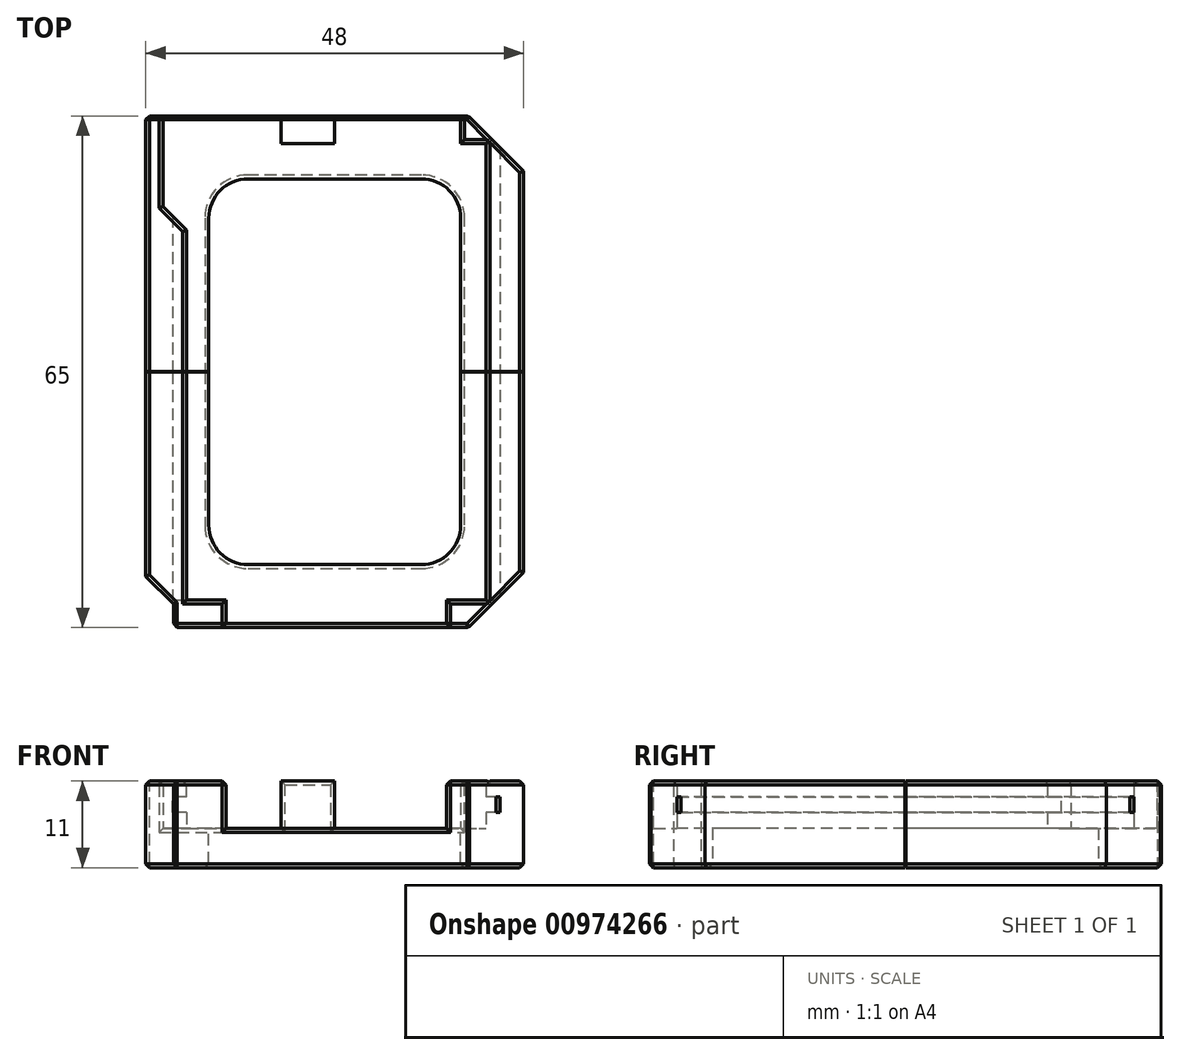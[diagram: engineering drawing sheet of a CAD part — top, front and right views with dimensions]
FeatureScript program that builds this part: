
annotation { "Feature Type Name" : "Feature", "Feature Type Description" : "" }
export const myFeature = defineFeature(function(context is Context, id is Id, definition is map)
    precondition{}
    {
        {
            var Q0;
            Q0=qCreatedBy(makeId("Top.planeOp"),FACE);
            cPlane(context, id + "F0", {"entities" : qUnion([Q0]), "cplaneType" : CPlaneType.OFFSET, "offset" : 7 * mm, "width" : 150 * mm, "height" : 150 * mm});
        }
        {
            var Q0;
            Q0=qCreatedBy(makeId("Top.planeOp"),FACE);
            cPlane(context, id + "F1", {"entities" : qUnion([Q0]), "cplaneType" : CPlaneType.OFFSET, "offset" : 5 * mm, "width" : 150 * mm, "height" : 150 * mm});
        }
        {
            var Q0;
            Q0=qCreatedBy(makeId("Top.planeOp"),FACE);
            cPlane(context, id + "F2", {"entities" : qUnion([Q0]), "cplaneType" : CPlaneType.OFFSET, "offset" : 2 * mm, "oppositeDirection" : true, "width" : 150 * mm, "height" : 150 * mm});
        }
        {
            var Q0;
            Q0=qCreatedBy(makeId("Top.planeOp"),FACE);
            var sketch = newSketch(context, id + "F3", { "sketchPlane" : qUnion([Q0])});
            skLineSegment(sketch, "E0", {"start": v(0, 0) * mm, "end": v(10, 0) * mm, "construction": true});
            skLineSegment(sketch, "E1.bottom", {"start": v(10, 0) * mm, "end": v(13.5, 0) * mm, "construction": true});
            skLineSegment(sketch, "E1.top", {"start": v(10, 65) * mm, "end": v(51, 65) * mm});
            skLineSegment(sketch, "E1.left", {"start": v(10, 0) * mm, "end": v(10, 6.5) * mm, "construction": true});
            skLineSegment(sketch, "E1.right", {"start": v(58, 7) * mm, "end": v(58, 58) * mm});
            skCircle(sketch, "E2", {"center": v(10, 3) * mm, "radius": 3 * mm, "construction": true});
            skLineSegment(sketch, "E3", {"start": v(13.5, 3) * mm, "end": v(13.5, 0) * mm});
            skLineSegment(sketch, "E4", {"start": v(13.5, 3) * mm, "end": v(10, 3) * mm, "construction": true});
            skArc(sketch, "E5", {"start": v(13.5, 3) * mm, "mid": v(12.47, 5.47) * mm, "end": v(10, 6.5) * mm, "construction": true});
            skLineSegment(sketch, "E6", {"start": v(10, 6.5) * mm, "end": v(10, 65) * mm});
            skLineSegment(sketch, "E7", {"start": v(13.5, 0) * mm, "end": v(51, 0) * mm});
            skPoint(sketch, "E8.visualSharp", {"position": v(58, 65) * mm});
            skArc(sketch, "E8.filletArc", {"start": v(58, 58) * mm, "mid": v(55.95, 62.95) * mm, "end": v(51, 65) * mm, "construction": true});
            skPoint(sketch, "E9.visualSharp", {"position": v(58, 0) * mm});
            skArc(sketch, "E9.filletArc", {"start": v(51, 0) * mm, "mid": v(55.95, 2.05) * mm, "end": v(58, 7) * mm, "construction": true});
            skLineSegment(sketch, "E10", {"start": v(51, 65) * mm, "end": v(58, 58) * mm});
            skLineSegment(sketch, "E11", {"start": v(51, 0) * mm, "end": v(58, 7) * mm});
            skLineSegment(sketch, "E12", {"start": v(10, 6.5) * mm, "end": v(13.5, 3) * mm});
            skSolve(sketch);
        }
        {
            var Q0;
            Q0 = qSketchRegion(id + "F3", true);
            extrude(context, id + "F4", {"entities" : qUnion([Q0]), "depth" : 11 * mm, "offsetDistance" : 25 * mm});
        }
        {
            var Q0;
            Q0=qCreatedBy(id+"F2.planeOp",FACE);
            var sketch = newSketch(context, id + "F5", { "sketchPlane" : qUnion([Q0])});
            skLineSegment(sketch, "E13.bottom", {"start": v(18, 57) * mm, "end": v(50, 57) * mm});
            skLineSegment(sketch, "E13.top", {"start": v(18, 8) * mm, "end": v(50, 8) * mm});
            skLineSegment(sketch, "E13.left", {"start": v(18, 57) * mm, "end": v(18, 8) * mm});
            skLineSegment(sketch, "E13.right", {"start": v(50, 57) * mm, "end": v(50, 8) * mm});
            skLineSegment(sketch, "E14.0", {"start": v(13.5, 0) * mm, "end": v(13.5, 0) * mm});
            skLineSegment(sketch, "E15.0", {"start": v(58, 7) * mm, "end": v(58, 7) * mm});
            skLineSegment(sketch, "E16.0", {"start": v(10, 65) * mm, "end": v(10, 65) * mm});
            skSolve(sketch);
        }
        {
            var Q0;
            Q0 = qSketchRegion(id + "F5", true);
            extrude(context, id + "F6", {"entities" : qUnion([Q0]), "operationType" : NewBodyOperationType.REMOVE, "depth" : 25 * mm, "offsetDistance" : 25 * mm});
        }
        {
            var Q0;
            Q0=makeQuery(id+"F6.boolean.opBoolean","COPY",EDGE,{"derivedFrom":makeQuery(id+"F6.opExtrude","SWEPT_EDGE",EDGE,{"disambiguationData":[OSD([sQuery(id+"F5.wireOp",EDGE,"E13.bottom"),sQuery(id+"F5.wireOp",EDGE,"E13.left")])]})});
            var Q1;
            Q1=makeQuery(id+"F6.boolean.opBoolean","COPY",EDGE,{"derivedFrom":makeQuery(id+"F6.opExtrude","SWEPT_EDGE",EDGE,{"disambiguationData":[OSD([sQuery(id+"F5.wireOp",EDGE,"E13.bottom"),sQuery(id+"F5.wireOp",EDGE,"E13.right")])]})});
            var Q2;
            Q2=makeQuery(id+"F6.boolean.opBoolean","COPY",EDGE,{"derivedFrom":makeQuery(id+"F6.opExtrude","SWEPT_EDGE",EDGE,{"disambiguationData":[OSD([sQuery(id+"F5.wireOp",EDGE,"E13.top"),sQuery(id+"F5.wireOp",EDGE,"E13.right")])]})});
            var Q3;
            Q3=makeQuery(id+"F6.boolean.opBoolean","COPY",EDGE,{"derivedFrom":makeQuery(id+"F6.opExtrude","SWEPT_EDGE",EDGE,{"disambiguationData":[OSD([sQuery(id+"F5.wireOp",EDGE,"E13.top"),sQuery(id+"F5.wireOp",EDGE,"E13.left")])]})});
            fillet(context, id + "F7", {"entities" : qUnion([Q0, Q1, Q2, Q3]), "radius" : 5 * mm, "tangentPropagation" : true, "allowEdgeOverflow" : false});
        }
        {
            var Q0;
            Q0=qCreatedBy(id+"F0.planeOp",FACE);
            var sketch = newSketch(context, id + "F8", { "sketchPlane" : qUnion([Q0])});
            skLineSegment(sketch, "E17.bottom", {"start": v(13.4, 61.5) * mm, "end": v(55, 61.5) * mm});
            skLineSegment(sketch, "E17.top", {"start": v(13.4, 3.5) * mm, "end": v(55, 3.5) * mm});
            skLineSegment(sketch, "E17.left", {"start": v(13.4, 61.5) * mm, "end": v(13.4, 3.5) * mm});
            skLineSegment(sketch, "E17.right", {"start": v(55, 61.5) * mm, "end": v(55, 3.5) * mm});
            skSolve(sketch);
        }
        {
            var Q0;
            Q0 = qSketchRegion(id + "F8", true);
            extrude(context, id + "F9", {"entities" : qUnion([Q0]), "operationType" : NewBodyOperationType.REMOVE, "depth" : 2 * mm, "offsetDistance" : 25 * mm});
        }
        {
            var Q0;
            Q0=qCreatedBy(id+"F1.planeOp",FACE);
            var sketch = newSketch(context, id + "F10", { "sketchPlane" : qUnion([Q0])});
            skLineSegment(sketch, "E18.bottom", {"start": v(27.2, 61.5) * mm, "end": v(34, 61.5) * mm});
            skLineSegment(sketch, "E18.top", {"start": v(15.2, 3.5) * mm, "end": v(20.2, 3.5) * mm});
            skLineSegment(sketch, "E18.left", {"start": v(15.2, 50.5) * mm, "end": v(15.2, 3.5) * mm});
            skLineSegment(sketch, "E18.right", {"start": v(53.2, 61.5) * mm, "end": v(53.2, 3.5) * mm});
            skLineSegment(sketch, "E19.0", {"start": v(10, 65) * mm, "end": v(10, 65) * mm});
            skLineSegment(sketch, "E20.0", {"start": v(58, 7) * mm, "end": v(58, 7) * mm});
            skLineSegment(sketch, "E21", {"start": v(12.2, 53.5) * mm, "end": v(12.2, 65.5) * mm});
            skLineSegment(sketch, "E22", {"start": v(12.2, 65.5) * mm, "end": v(27.2, 65.5) * mm});
            skLineSegment(sketch, "E23", {"start": v(27.2, 65.5) * mm, "end": v(27.2, 61.5) * mm});
            skLineSegment(sketch, "E24", {"start": v(34, 61.5) * mm, "end": v(34, 65.5) * mm});
            skLineSegment(sketch, "E25", {"start": v(34, 65.5) * mm, "end": v(50, 65.5) * mm});
            skLineSegment(sketch, "E26", {"start": v(50, 65.5) * mm, "end": v(50, 61.5) * mm});
            skLineSegment(sketch, "E27.trimOffspring", {"start": v(50, 61.5) * mm, "end": v(53.2, 61.5) * mm});
            skLineSegment(sketch, "E28", {"start": v(20.2, 3.5) * mm, "end": v(20.2, -0.5) * mm});
            skLineSegment(sketch, "E29", {"start": v(20.2, -0.5) * mm, "end": v(48.2, -0.5) * mm});
            skLineSegment(sketch, "E30", {"start": v(48.2, -0.5) * mm, "end": v(48.2, 3.5) * mm});
            skLineSegment(sketch, "E31.trimOffspring", {"start": v(48.2, 3.5) * mm, "end": v(53.2, 3.5) * mm});
            skLineSegment(sketch, "E32", {"start": v(12.2, 53.5) * mm, "end": v(15.2, 50.5) * mm});
            skSolve(sketch);
        }
        {
            var Q0;
            Q0 = qSketchRegion(id + "F10", true);
            extrude(context, id + "F11", {"entities" : qUnion([Q0]), "operationType" : NewBodyOperationType.REMOVE, "depth" : 8 * mm, "offsetDistance" : 25 * mm});
        }
        {
            var Q0;
            Q0=makeQuery(id+"F4.opExtrude","SWEPT_FACE",FACE,{"disambiguationData":[OSD([sQuery(id+"F3.wireOp",EDGE,"E7")])]});
            var Q1;
            Q1=makeQuery(id+"F4.opExtrude","SWEPT_FACE",FACE,{"disambiguationData":[OSD([sQuery(id+"F3.wireOp",EDGE,"E1.top")])]});
            var Q2;
            {var subQ0=sQuery(id+"F3.wireOp",EDGE,"E7");var subQ1=sQuery(id+"F3.wireOp",EDGE,"E1.top");var subQ2=sQuery(id+"F3.wireOp",EDGE,"E5");var subQ3=sQuery(id+"F3.wireOp",EDGE,"E3");var subQ4=sQuery(id+"F3.wireOp",EDGE,"E6");Q2=makeQuery(id+"F11.boolean.opBoolean","SPLIT",FACE,{"disambiguationData":[TD([makeQuery(id+"F4.opExtrude","SWEPT_FACE",FACE,{"disambiguationData":[OSD([subQ3])]})])],"derivedFrom":makeQuery(id+"F4.opExtrude","CAP_FACE",FACE,{"disambiguationData":[OSD([subQ1,sQuery(id+"F3.wireOp",EDGE,"E1.right"),subQ3,subQ2,subQ4,subQ0,sQuery(id+"F3.wireOp",EDGE,"E10"),sQuery(id+"F3.wireOp",EDGE,"E11")])],"isStart":false})});}
            var Q3;
            {var subQ0=sQuery(id+"F3.wireOp",EDGE,"E11");var subQ1=sQuery(id+"F3.wireOp",EDGE,"E1.top");var subQ2=sQuery(id+"F3.wireOp",EDGE,"E1.right");var subQ3=sQuery(id+"F3.wireOp",EDGE,"E10");var subQ4=sQuery(id+"F3.wireOp",EDGE,"E7");Q3=makeQuery(id+"F11.boolean.opBoolean","SPLIT",FACE,{"disambiguationData":[TD([makeQuery(id+"F4.opExtrude","SWEPT_FACE",FACE,{"disambiguationData":[OSD([subQ2])]})])],"derivedFrom":makeQuery(id+"F4.opExtrude","CAP_FACE",FACE,{"disambiguationData":[OSD([subQ1,subQ2,sQuery(id+"F3.wireOp",EDGE,"E3"),sQuery(id+"F3.wireOp",EDGE,"E5"),sQuery(id+"F3.wireOp",EDGE,"E6"),subQ4,subQ3,subQ0])],"isStart":false})});}
            var Q4;
            Q4=makeQuery(id+"F4.opExtrude","CAP_FACE",FACE,{"disambiguationData":[OSD([sQuery(id+"F3.wireOp",EDGE,"E1.top"),sQuery(id+"F3.wireOp",EDGE,"E1.right"),sQuery(id+"F3.wireOp",EDGE,"E3"),sQuery(id+"F3.wireOp",EDGE,"E5"),sQuery(id+"F3.wireOp",EDGE,"E6"),sQuery(id+"F3.wireOp",EDGE,"E7"),sQuery(id+"F3.wireOp",EDGE,"E10"),sQuery(id+"F3.wireOp",EDGE,"E11")])],"isStart":true});
            chamfer(context, id + "F12", {"entities" : qUnion([Q0, Q1, Q2, Q3, Q4]), "width" : .5 * mm, "tangentPropagation" : true});
        }
        {
            var Q0;
            Q0=qCreatedBy(id+"F2.planeOp",FACE);
            var sketch = newSketch(context, id + "F13", { "sketchPlane" : qUnion([Q0])});
            skLineSegment(sketch, "E33.bottom", {"start": v(0, 32.45) * mm, "end": v(66, 32.45) * mm});
            skLineSegment(sketch, "E33.top", {"start": v(0, 32.55) * mm, "end": v(66, 32.55) * mm});
            skLineSegment(sketch, "E33.left", {"start": v(0, 32.5) * mm, "end": v(0, 32.45) * mm});
            skLineSegment(sketch, "E33.right", {"start": v(66, 32.55) * mm, "end": v(66, 32.45) * mm});
            skLineSegment(sketch, "E34", {"start": v(0, 32.55) * mm, "end": v(0, 32.5) * mm});
            skSolve(sketch);
        }
        {
            var Q0;
            Q0 = qSketchRegion(id + "F13", true);
            extrude(context, id + "F14", {"entities" : qUnion([Q0]), "operationType" : NewBodyOperationType.REMOVE, "depth" : 25 * mm, "offsetDistance" : 25 * mm});
        }
    });
